# Revit family: Kitchen_Faucet-LIXIL-AS-Aspiration_Pull_Down_Touchless-104880
name_source: partatom
category: Plumbing Fixtures
units: mm (PartAtom-declared; Revit-internal decimal feet)

## family parameters
Cut with Voids When Loaded = No
Enable Cutting in Views = Yes
Host = Face
Maintain Annotation Orientation = No
OmniClass Number = 23.45.55.17
OmniClass Title = Mixing Faucets
Part Type = Normal
Room Calculation Point = No
Round Connector Dimension = Use Diameter
Shared = No

## types (6) — shared parameters
Assembly Code = D2010400
Brand = American Standard
CW Connection = Yes
Cold Water Connection Diameter = 0"
Collection = Aspiration™
Default Elevation = 0"
Depth = 10 5/8"
Description = Pull-Down Kitchen Faucet
Flow Rate = 2 GPM
HW Connection = Yes
Height = 18 5/16"
Hole Size = 1 3/8"
Hot Water Connection Diameter = 0"
Keynote = 22 40 00
Manufacturer = LIXIL
Maximum Deck Thickness = 3 1/4"
Product Documentation Link = Contact Manufacturer for More Information
Product Name = Pull-Down Kitchen Faucet With Selectronic® Hands-Free Technology
Product Page URL = Contact Manufacturer for More Information
URL = https://www.americanstandard-us.com
Vent Connection = No
Version = 2023 - v1.0a
Warranty URL = Contact Manufacturer for More Information
Waste Connection = No
Width = 2 1/4"

## per-type parameters (varying)
| type | Accent Finish | Finish | Model | Rubber Finish |
| Polished Chrome | Metal - American Standard - Chrome | Metal - American Standard - Chrome | 104880000 | Rubber - American Standard - White |
| Stainless Steel | Metal - American Standard - Chrome | Metal - American Standard - Stainless Steel | 104880DC0 | Rubber - American Standard - White |
| Matte Black | Metal - American Standard - Matte Black | Metal - American Standard - Matte Black | 104880243 | Rubber - American Standard - Black |
| Brushed Cool Sunrise | Metal - American Standard - Brushed Cool Sunrise | Metal - American Standard - Brushed Cool Sunrise | 104880GN0 | Rubber - American Standard - Black |
| Matte Black / Brushed Cool Sunrise | Metal - American Standard - Brushed Cool Sunrise | Metal - American Standard - Matte Black | 104880424 | Rubber - American Standard - Black |
| Matte Black / Stainless | Metal - American Standard - Stainless Steel | Metal - American Standard - Matte Black | 104880423 | Rubber - American Standard - Black |

## geometry (parser evidence)
native form markers: Sweep x2
no freeform markers — native parametric forms only
